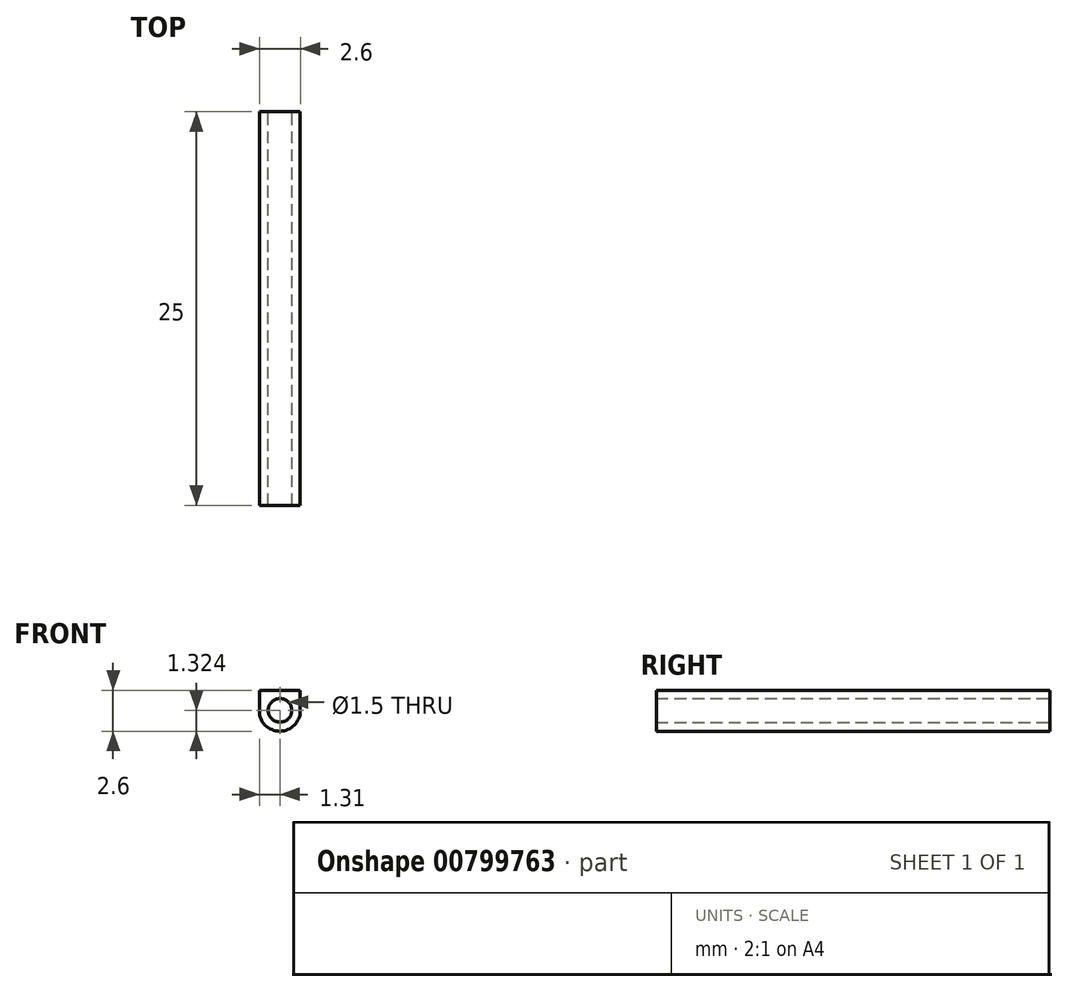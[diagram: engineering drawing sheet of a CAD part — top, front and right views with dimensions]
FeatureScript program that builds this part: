
annotation { "Feature Type Name" : "Feature", "Feature Type Description" : "" }
export const myFeature = defineFeature(function(context is Context, id is Id, definition is map)
    precondition{}
    {
        {
            var Q0;
            Q0=qCreatedBy(makeId("Front.planeOp"),FACE);
            var sketch = newSketch(context, id + "F0", { "sketchPlane" : qUnion([Q0])});
            skLineSegment(sketch, "E0", {"start": v(-1.31, 0) * mm, "end": v(1.29, 0) * mm});
            skLineSegment(sketch, "E1", {"start": v(1.29, 0) * mm, "end": v(1.29, -1.3) * mm});
            skLineSegment(sketch, "E2", {"start": v(-1.31, 0) * mm, "end": v(-1.31, -1.3) * mm});
            skArc(sketch, "E3", {"start": v(-1.31, -1.3) * mm, "mid": v(-0.01, -2.6) * mm, "end": v(1.29, -1.3) * mm});
            skSolve(sketch);
        }
        {
            var Q0;
            Q0=makeQuery(id+"F0.imprint","IMPRINT",FACE,{"disambiguationData":[TD([[makeQuery(id+"F0.imprint","IMPRINT",EDGE,{"derivedFrom":sQuery(id+"F0.wireOp",EDGE,"E0")}),-1.0]])]});
            extrude(context, id + "F1", {"entities" : qUnion([Q0]), "depth" : 25 * mm, "offsetDistance" : 25 * mm});
        }
        {
            var Q0;
            Q0=qCreatedBy(makeId("Front.planeOp"),FACE);
            var sketch = newSketch(context, id + "F2", { "sketchPlane" : qUnion([Q0])});
            skCircle(sketch, "E4", {"center": v(0, -1.28) * mm, "radius": 0.75 * mm});
            skSolve(sketch);
        }
        {
            var Q0;
            Q0 = qSketchRegion(id + "F2", true);
            extrude(context, id + "F3", {"entities" : qUnion([Q0]), "operationType" : NewBodyOperationType.REMOVE, "depth" : 25 * mm, "offsetDistance" : 25 * mm});
        }
    });
